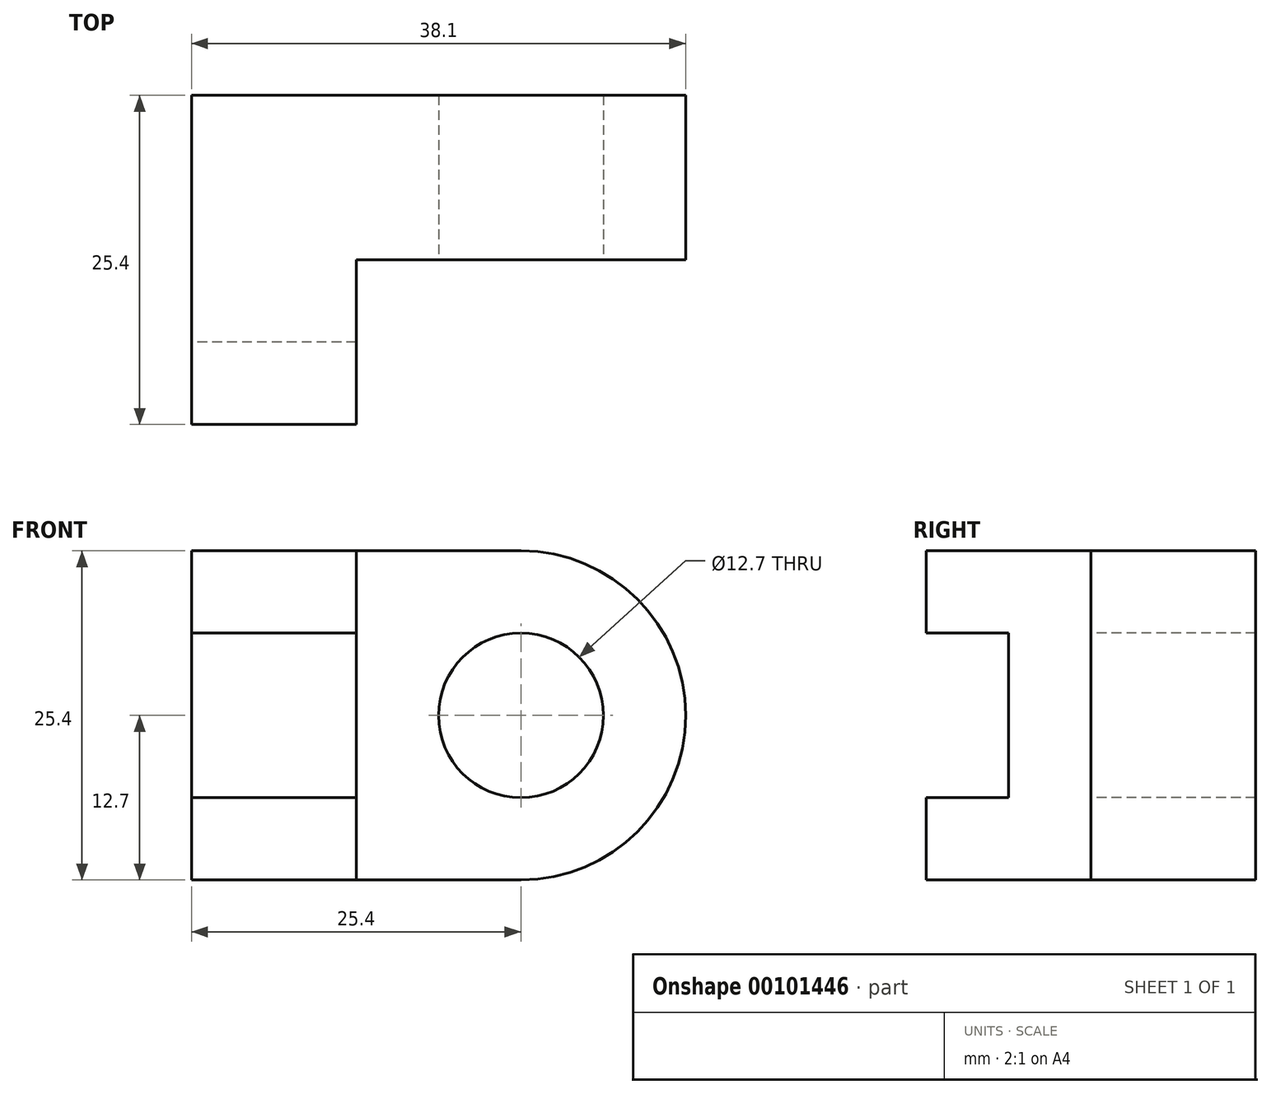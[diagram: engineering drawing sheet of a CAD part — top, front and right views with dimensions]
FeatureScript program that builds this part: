
annotation { "Feature Type Name" : "Feature", "Feature Type Description" : "" }
export const myFeature = defineFeature(function(context is Context, id is Id, definition is map)
    precondition{}
    {
        {
            var Q0;
            Q0=qCreatedBy(makeId("Front.planeOp"),FACE);
            var sketch = newSketch(context, id + "F0", { "sketchPlane" : qUnion([Q0])});
            skLineSegment(sketch, "E0", {"start": v(0, 0) * mm, "end": v(0, 25.4) * mm});
            skLineSegment(sketch, "E1", {"start": v(0, 25.4) * mm, "end": v(25.4, 25.4) * mm});
            skLineSegment(sketch, "E2", {"start": v(0, 0) * mm, "end": v(25.4, 0) * mm});
            skArc(sketch, "E3", {"start": v(25.4, 0) * mm, "mid": v(38.1, 12.7) * mm, "end": v(25.4, 25.4) * mm});
            skCircle(sketch, "E4", {"center": v(25.4, 12.7) * mm, "radius": 6.35 * mm});
            skSolve(sketch);
        }
        {
            var Q0;
            Q0 = qSketchRegion(id + "F0", true);
            extrude(context, id + "F1", {"entities" : qUnion([Q0]), "oppositeDirection" : true, "depth" : 12.7 * mm});
        }
        {
            var Q0;
            Q0=qCreatedBy(makeId("Right.planeOp"),FACE);
            var sketch = newSketch(context, id + "F2", { "sketchPlane" : qUnion([Q0])});
            skLineSegment(sketch, "E5", {"start": v(0, 0) * mm, "end": v(0, 25.4) * mm});
            skLineSegment(sketch, "E6", {"start": v(0, 25.4) * mm, "end": v(-12.7, 25.4) * mm});
            skLineSegment(sketch, "E7", {"start": v(-12.7, 25.4) * mm, "end": v(-12.7, 19.05) * mm});
            skLineSegment(sketch, "E8", {"start": v(-12.7, 19.05) * mm, "end": v(-6.35, 19.05) * mm});
            skLineSegment(sketch, "E9", {"start": v(-6.35, 19.05) * mm, "end": v(-6.35, 6.35) * mm});
            skLineSegment(sketch, "E10", {"start": v(-6.35, 6.35) * mm, "end": v(-12.7, 6.35) * mm});
            skLineSegment(sketch, "E11", {"start": v(-12.7, 6.35) * mm, "end": v(-12.7, 0) * mm});
            skLineSegment(sketch, "E12", {"start": v(-12.7, 0) * mm, "end": v(0, 0) * mm});
            skSolve(sketch);
        }
        {
            var Q0;
            Q0 = qSketchRegion(id + "F2", true);
            extrude(context, id + "F3", {"entities" : qUnion([Q0]), "operationType" : NewBodyOperationType.ADD, "depth" : 12.7 * mm});
        }
    });
